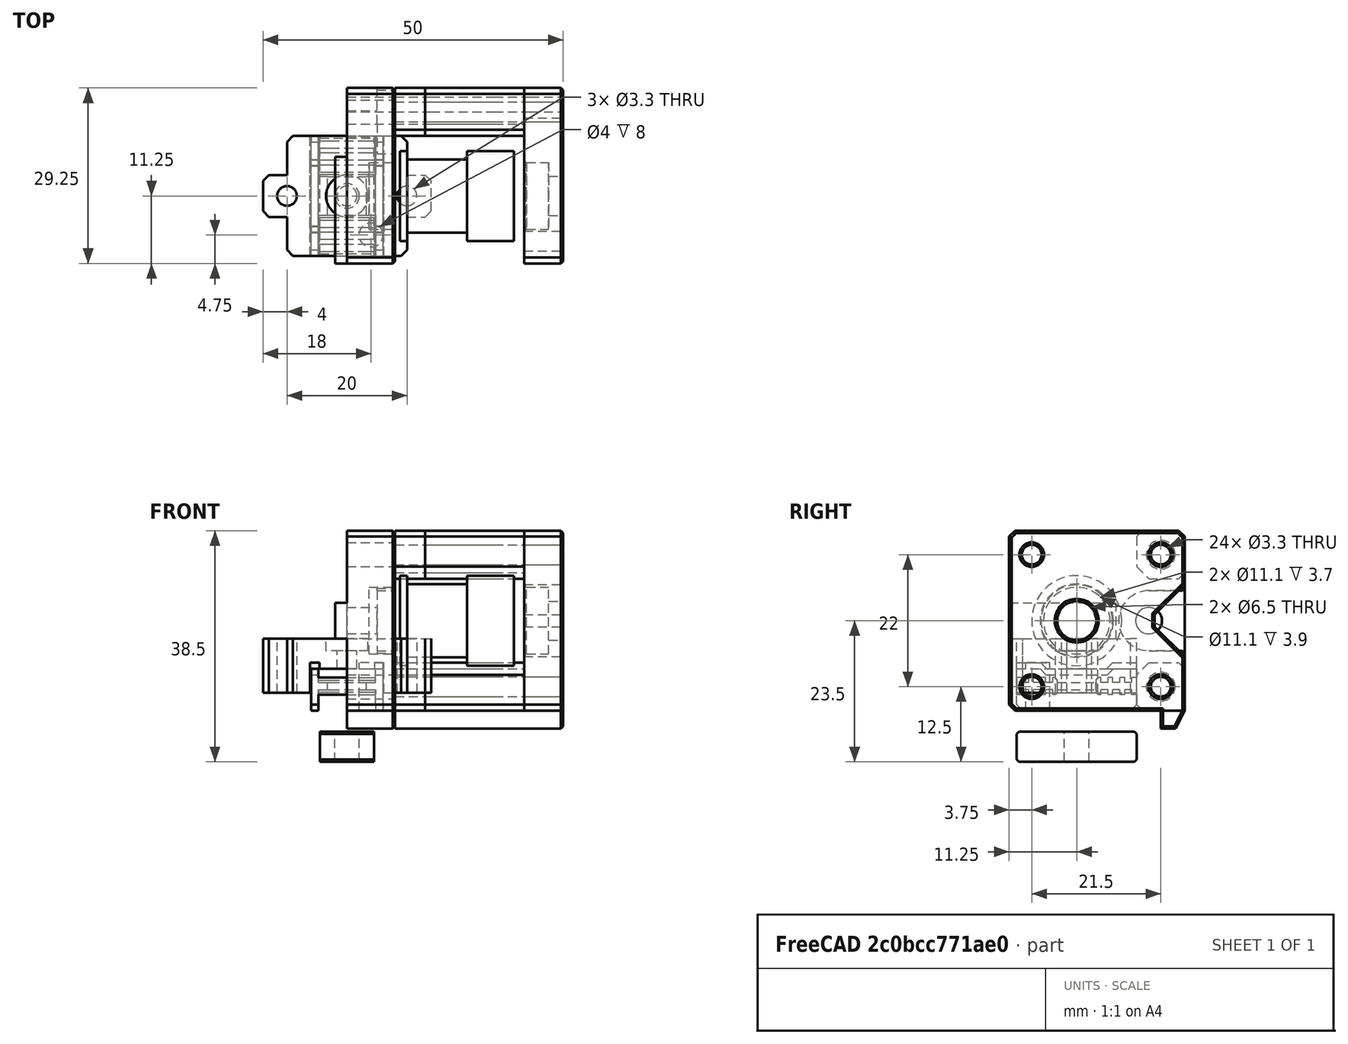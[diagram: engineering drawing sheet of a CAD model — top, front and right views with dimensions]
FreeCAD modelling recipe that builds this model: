
FCSTD DOCUMENT  (FreeCAD 0.18R16146 (Git))
Label: 9mm-belt-mod
License: Other
LicenseURL: GPL3
objects: Part::Feature×11, Part::Box×9, Part::MultiFuse×6, Part::Cylinder×5, Part::Cut×4, Part::MultiCommon×3, Part::Chamfer×2
note: 40 computed .brp shape members not serialized (recipe doc carries the construction recipe); baked Part::Feature solids carry a one-line shape summary decoded from their .brp

FEATURE [Part::Feature] Chamfer004013006001  label="belt-holder001"
  shape: bbox 12 x 20 x 7 mm, 80 faces (baked)
FEATURE [Part::Feature] Chamfer004013007013  label="belt-connector003"
  shape: bbox 28 x 20 x 9 mm, 43 faces (baked)
FEATURE [Part::Box] Box  label="Cube"
  AttacherType = Attacher::AttachEngine3D
  Height = 4
  Length = 1.5
  Placement = pos=(-4.75,-10.5,4.7) rot=(0,0,1;0rad)
  Width = 21
FEATURE [Part::Box] Box001  label="Cube001"
  AttacherType = Attacher::AttachEngine3D
  Height = 4
  Length = 1.5
  Placement = pos=(3.25,-10.5,4.7) rot=(0,0,1;0rad)
  Width = 21
FEATURE [Part::MultiFuse] Fusion
  Shapes = -> [Box,Box001]
FEATURE [Part::Feature] Fusion001
  Placement = pos=(0,0,-5.2) rot=(0,0,1;0rad)
  shape: bbox 9.5 x 21 x 4 mm, 12 faces, 2 solids (baked)
FEATURE [Part::MultiFuse] Fusion002
  Shapes = -> [Fusion001,Fusion]
FEATURE [Part::Cut] Cut
  Base = -> Chamfer004013006001
  Tool = -> Fusion002
FEATURE [Part::Box] Box002  label="Cube002"
  AttacherType = Attacher::AttachEngine3D
  Height = 5
  Length = 2
  Placement = pos=(-1,-11,1.7) rot=(0,0,1;0rad)
  Width = 22
FEATURE [Part::Feature] Cut001
  shape: bbox 12 x 20 x 7 mm, 120 faces (baked)
FEATURE [Part::MultiCommon] Common
  Placement = pos=(-3.75,0,0) rot=(0,0,1;0rad)
  Shapes = -> [Box002,Cut001]
FEATURE [Part::Feature] Common001
  Placement = pos=(3.75,0,0) rot=(0,0,1;0rad)
  shape: bbox 2 x 20 x 2.8 mm, 64 faces, 2 solids (baked)
FEATURE [Part::MultiFuse] Fusion003  label="belt-mounter-9mm"
  Shapes = -> [Common001,Common,Cut]
FEATURE [Part::Box] Box003  label="Cube003"
  AttacherType = Attacher::AttachEngine3D
  Height = 1
  Length = 2
  Placement = pos=(2.6,-10,7) rot=(0,0,1;0rad)
  Width = 20
FEATURE [Part::Box] Box004  label="Cube004"
  AttacherType = Attacher::AttachEngine3D
  Height = 1
  Length = 2
  Placement = pos=(-4.6,-10,7) rot=(0,0,1;0rad)
  Width = 20
FEATURE [Part::MultiFuse] Fusion004  label="belt-holder-9mm"
  Shapes = -> [Chamfer004013007013,Box003,Box004]
FEATURE [Part::Feature] Chamfer024034004003001  label="spacer-exp001"
  Placement = pos=(40,-32.5,0) rot=(0,0,1;0rad)
  shape: bbox 28 x 29.25 x 33 mm, 55 faces (baked)
FEATURE [Part::Feature] Chamfer024034004004001  label="back-plate-std"
  Placement = pos=(40,-32.5,0) rot=(0,0,1;0rad)
  shape: bbox 10 x 29.25 x 33 mm, 43 faces (baked)
FEATURE [Part::Box] Box005  label="Cube005"
  AttacherType = Attacher::AttachEngine3D
  Height = 5
  Length = 9
  Placement = pos=(-4.5,-10,-8.5) rot=(0,0,1;0rad)
  Width = 20
FEATURE [Part::Cylinder] Cylinder
  Angle = 360
  AttacherType = Attacher::AttachEngine3D
  Height = 10
  Placement = pos=(0,0,-10.5) rot=(0,0,1;0rad)
  Radius = 2.05
FEATURE [Part::Chamfer] Chamfer
  Base = -> Box005
  Edges = 4 edges r=0.4: [Edge9,Edge10,Edge11,Edge12]
FEATURE [Part::Cut] Cut002  label="belt-nut"
  Base = -> Chamfer
  Tool = -> Cylinder
FEATURE [Part::Cylinder] Cylinder001
  Angle = 360
  AttacherType = Attacher::AttachEngine3D
  Height = 10
  Placement = pos=(5,0,1e-15) rot=(0,-1,0;1.5708rad)
  Radius = 6.1
FEATURE [Part::Cylinder] Cylinder002
  Angle = 360
  AttacherType = Attacher::AttachEngine3D
  Height = 1.2
  Placement = pos=(-5,0,-1e-15) rot=(0,-1,0;1.5708rad)
  Radius = 7.5
FEATURE [Part::Cylinder] Cylinder003
  Angle = 360
  AttacherType = Attacher::AttachEngine3D
  Height = 7.8
  Placement = pos=(12.8,0,-5e-15) rot=(0,-1,0;1.5708rad)
  Radius = 7.5
FEATURE [Part::MultiFuse] Fusion005  label="gate-pulley"
  Placement = pos=(15,0,15) rot=(0,0,1;0rad)
  Shapes = -> [Cylinder003,Cylinder002,Cylinder001]
FEATURE [Part::Box] Box006  label="Cube006"
  AttacherType = Attacher::AttachEngine3D
  Height = 35
  Length = 16.5
  Placement = pos=(8,-16,-4) rot=(0,0,1;0rad)
  Width = 36
FEATURE [Part::Box] Box007  label="Cube007"
  AttacherType = Attacher::AttachEngine3D
  Height = 39
  Length = 16.5
  Placement = pos=(24.5,-16,-7) rot=(0,0,1;0rad)
  Width = 36
FEATURE [Part::Feature] Chamfer024034004004002  label="spacer-exp002"
  Placement = pos=(40,-32.5,0) rot=(0,0,1;0rad)
  shape: bbox 28 x 29.25 x 33 mm, 55 faces (baked)
FEATURE [Part::Box] Box008  label="Cube008"
  AttacherType = Attacher::AttachEngine3D
  Height = 51
  Length = 10
  Placement = pos=(19.5,-12.5,-7) rot=(0,0,1;0rad)
  Width = 35
FEATURE [Part::Feature] Common003001  label="Common004"
  Placement = pos=(5,0,0) rot=(0,0,1;0rad)
  shape: bbox 16.5 x 8 x 30 mm, 22 faces, 2 solids (baked)
FEATURE [Part::Cylinder] Cylinder004
  Angle = 360
  AttacherType = Attacher::AttachEngine3D
  Height = 10
  Placement = pos=(23.6,0,15) rot=(0,1,0;1.5708rad)
  Radius = 5.55
FEATURE [Part::Feature] Chamfer024034004004003001  label="spacer-9mm001"
  shape: bbox 28 x 29.25 x 30 mm, 96 faces (baked)
FEATURE [Part::MultiCommon] Common003002
  Shapes = -> [Chamfer024034004004002,Box007]
FEATURE [Part::Cut] Cut003
  Base = -> Common003002
  Tool = -> Box008
FEATURE [Part::Cut] Cut004
  Base = -> Cut003
  Tool = -> Cylinder004
FEATURE [Part::Chamfer] Chamfer024034004004003002
  Base = -> Cut004
  Edges = 1 edges r=0.4: [Edge18]
FEATURE [Part::MultiCommon] Common003003
  Shapes = -> [Box006,Chamfer024034004003001]
FEATURE [Part::Feature] Common003003001  label="Common003004"
  Placement = pos=(6,0,0) rot=(0,0,1;0rad)
  shape: bbox 16.5 x 8 x 33 mm, 24 faces, 2 solids (baked)
FEATURE [Part::MultiFuse] Fusion006  label="9mm-spacer"
  Shapes = -> [Common003003,Common003003001,Chamfer024034004004003002]
